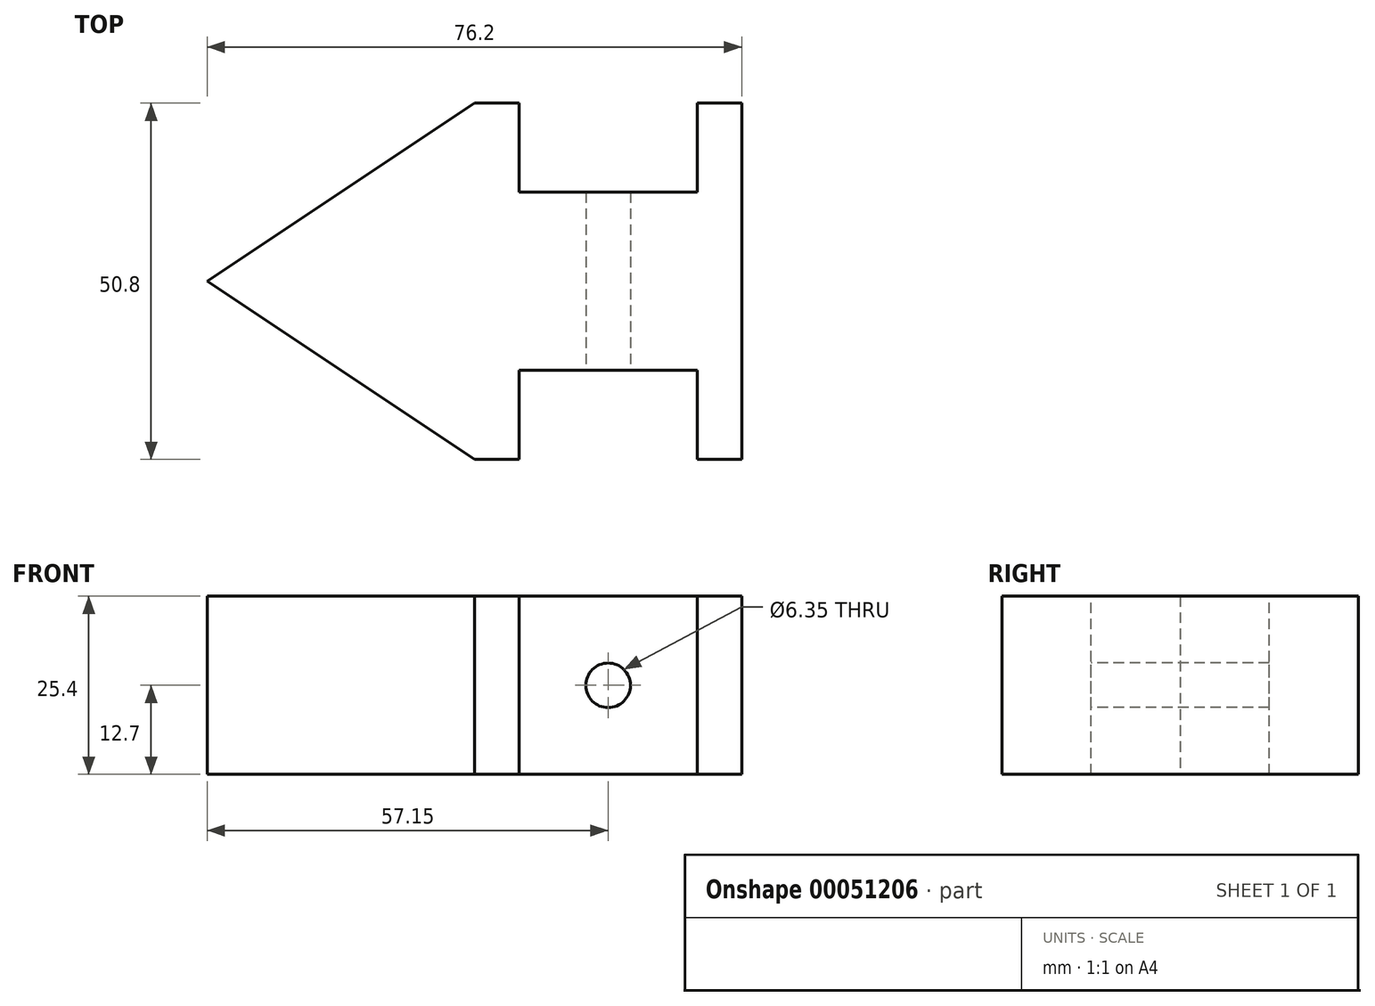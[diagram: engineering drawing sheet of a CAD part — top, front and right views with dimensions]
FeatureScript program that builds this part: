
annotation { "Feature Type Name" : "Feature", "Feature Type Description" : "" }
export const myFeature = defineFeature(function(context is Context, id is Id, definition is map)
    precondition{}
    {
        {
            var Q0;
            Q0=qCreatedBy(makeId("Top.planeOp"),FACE);
            var sketch = newSketch(context, id + "F0", { "sketchPlane" : qUnion([Q0])});
            skLineSegment(sketch, "E0", {"start": v(0, 0) * mm, "end": v(38.1, -25.4) * mm});
            skLineSegment(sketch, "E1", {"start": v(38.1, -25.4) * mm, "end": v(76.2, -25.4) * mm});
            skLineSegment(sketch, "E2", {"start": v(76.2, -25.4) * mm, "end": v(76.2, 0) * mm});
            skLineSegment(sketch, "E3", {"start": v(76.2, 0) * mm, "end": v(0, 0) * mm});
            skSolve(sketch);
        }
        {
            var Q0;
            Q0 = qSketchRegion(id + "F0", true);
            extrude(context, id + "F1", {"entities" : qUnion([Q0]), "depth" : 25.4 * mm});
        }
        {
            var Q0;
            Q0=makeQuery(id+"F1.opExtrude","CAP_FACE",FACE,{"disambiguationData":[OSD([sQuery(id+"F0.wireOp",EDGE,"E0"),sQuery(id+"F0.wireOp",EDGE,"E1"),sQuery(id+"F0.wireOp",EDGE,"E2"),sQuery(id+"F0.wireOp",EDGE,"E3")])],"isStart":false});
            var sketch = newSketch(context, id + "F2", { "sketchPlane" : qUnion([Q0])});
            skLineSegment(sketch, "E4.bottom", {"start": v(69.85, -25.4) * mm, "end": v(44.45, -25.4) * mm});
            skLineSegment(sketch, "E4.top", {"start": v(69.85, -12.7) * mm, "end": v(44.45, -12.7) * mm});
            skLineSegment(sketch, "E4.left", {"start": v(69.85, -25.4) * mm, "end": v(69.85, -12.7) * mm});
            skLineSegment(sketch, "E4.right", {"start": v(44.45, -25.4) * mm, "end": v(44.45, -12.7) * mm});
            skSolve(sketch);
        }
        {
            var Q0;
            Q0 = qSketchRegion(id + "F2", true);
            extrude(context, id + "F3", {"entities" : qUnion([Q0]), "operationType" : NewBodyOperationType.REMOVE, "oppositeDirection" : true, "depth" : 25.4 * mm});
        }
        {
            var Q0;
            Q0=makeQuery(id+"F3.boolean.opBoolean","COPY",FACE,{"derivedFrom":makeQuery(id+"F3.opExtrude","SWEPT_FACE",FACE,{"disambiguationData":[OSD([sQuery(id+"F2.wireOp",EDGE,"E4.top")])]})});
            var sketch = newSketch(context, id + "F4", { "sketchPlane" : qUnion([Q0])});
            skCircle(sketch, "E5", {"center": v(57.15, 12.7) * mm, "radius": 3.18 * mm});
            skPoint(sketch, "E5.centerSnap0", {"position": v(57.15, 25.4) * mm});
            skPoint(sketch, "E5.centerSnap1", {"position": v(44.45, 12.7) * mm});
            skSolve(sketch);
        }
        {
            var Q0;
            Q0 = qSketchRegion(id + "F4", true);
            extrude(context, id + "F5", {"entities" : qUnion([Q0]), "operationType" : NewBodyOperationType.REMOVE, "oppositeDirection" : true, "depth" : 12.7 * mm});
        }
        {
            var Q0;
            Q0=makeQuery(id+"F1.opExtrude","SWEPT_BODY",BODY,{"disambiguationData":[OSD([sQuery(id+"F0.wireOp",EDGE,"E0"),sQuery(id+"F0.wireOp",EDGE,"E1"),sQuery(id+"F0.wireOp",EDGE,"E2"),sQuery(id+"F0.wireOp",EDGE,"E3")])]});
            var Q1;
            Q1=qCreatedBy(makeId("Front.planeOp"),FACE);
            mirror(context, id + "F6", {"operationType" : NewBodyOperationType.ADD, "entities" : qUnion([Q0]), "mirrorPlane" : qUnion([Q1])});
        }
    });
